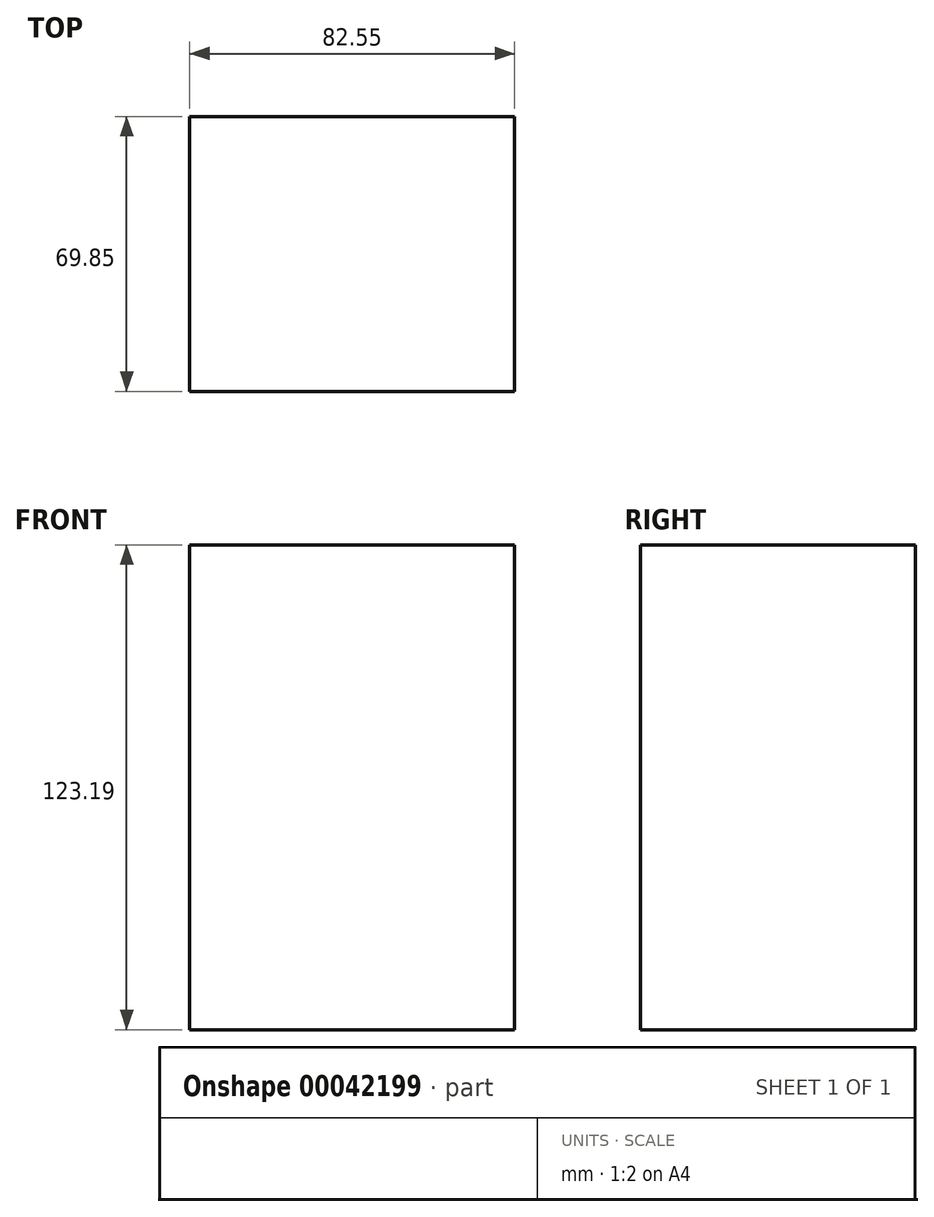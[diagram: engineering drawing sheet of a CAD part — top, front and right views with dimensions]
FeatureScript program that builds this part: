
annotation { "Feature Type Name" : "Feature", "Feature Type Description" : "" }
export const myFeature = defineFeature(function(context is Context, id is Id, definition is map)
    precondition{}
    {
        {
            var Q0;
            Q0=qCreatedBy(makeId("Front.planeOp"),FACE);
            var sketch = newSketch(context, id + "F0", { "sketchPlane" : qUnion([Q0])});
            skLineSegment(sketch, "E0.bottom", {"start": v(0, 0) * mm, "end": v(82.55, 0) * mm});
            skLineSegment(sketch, "E0.top", {"start": v(0, 123.19) * mm, "end": v(82.55, 123.19) * mm});
            skLineSegment(sketch, "E0.left", {"start": v(0, 0) * mm, "end": v(0, 123.19) * mm});
            skLineSegment(sketch, "E0.right", {"start": v(82.55, 0) * mm, "end": v(82.55, 123.19) * mm});
            skSolve(sketch);
        }
        {
            var Q0;
            Q0=makeQuery(id+"F0.imprint","IMPRINT",FACE,{"disambiguationData":[TD([[makeQuery(id+"F0.imprint","IMPRINT",EDGE,{"derivedFrom":sQuery(id+"F0.wireOp",EDGE,"E0.bottom")}),1.0]])]});
            extrude(context, id + "F1", {"entities" : qUnion([Q0]), "depth" : 69.85 * mm});
        }
    });
